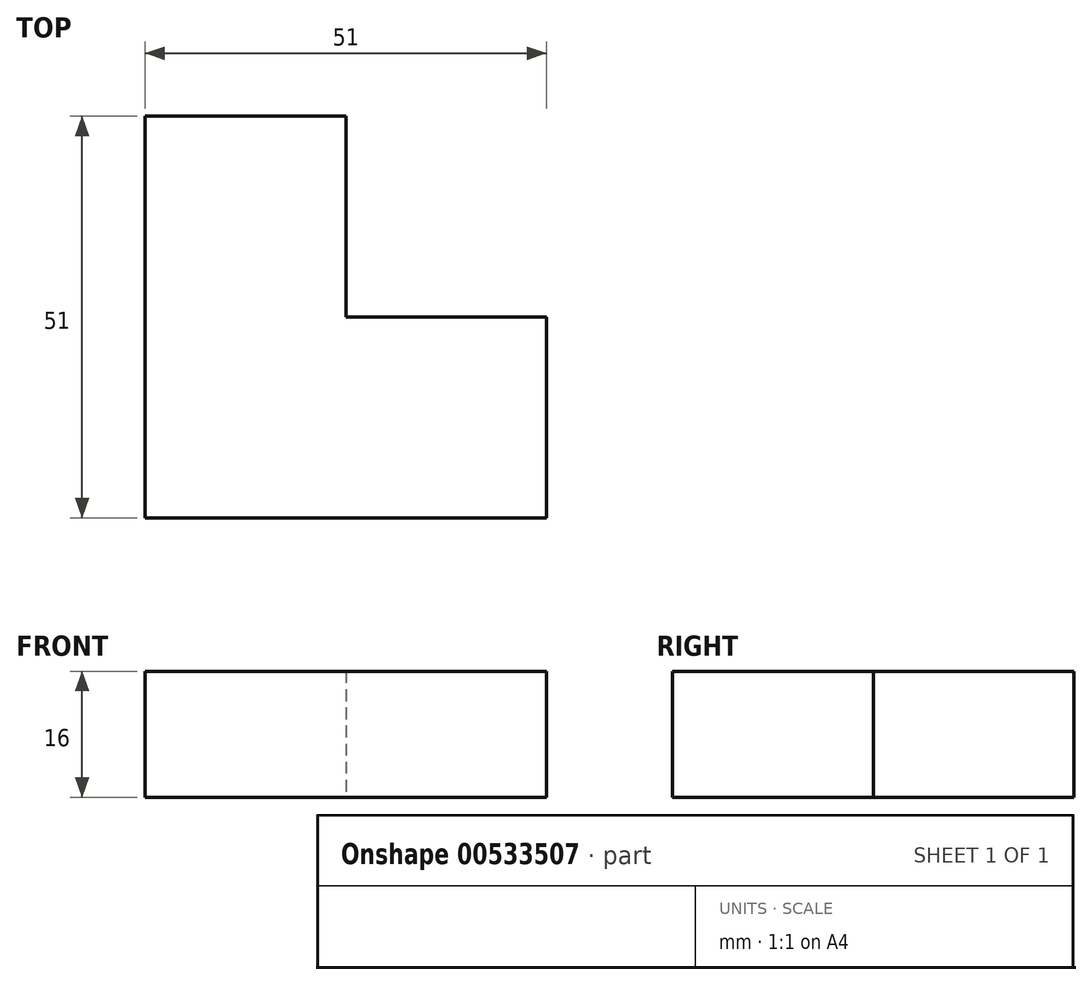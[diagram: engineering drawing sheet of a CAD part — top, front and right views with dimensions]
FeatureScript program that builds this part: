
annotation { "Feature Type Name" : "Feature", "Feature Type Description" : "" }
export const myFeature = defineFeature(function(context is Context, id is Id, definition is map)
    precondition{}
    {
        {
            var Q0;
            Q0=qCreatedBy(makeId("Top.planeOp"),FACE);
            var sketch = newSketch(context, id + "F0", { "sketchPlane" : qUnion([Q0])});
            skLineSegment(sketch, "E0.bottom", {"start": v(0, 0) * mm, "end": v(51, 0) * mm});
            skLineSegment(sketch, "E0.top", {"start": v(0, 51) * mm, "end": v(51, 51) * mm});
            skLineSegment(sketch, "E0.left", {"start": v(0, 0) * mm, "end": v(0, 51) * mm});
            skLineSegment(sketch, "E0.right", {"start": v(51, 0) * mm, "end": v(51, 51) * mm});
            skLineSegment(sketch, "E1", {"start": v(25.5, 51) * mm, "end": v(25.5, 25.5) * mm});
            skPoint(sketch, "E1.endSnap0", {"position": v(51, 25.5) * mm});
            skLineSegment(sketch, "E2", {"start": v(25.5, 25.5) * mm, "end": v(51, 25.5) * mm});
            skSolve(sketch);
        }
        {
            var Q0;
            {var subQ1=sQuery(id+"F0.wireOp",EDGE,"E0.bottom");Q0=makeQuery(id+"F0.imprint","IMPRINT",FACE,{"disambiguationData":[TD([[makeQuery(id+"F0.imprint","IMPRINT",EDGE,{"derivedFrom":subQ1}),1.0]])]});}
            extrude(context, id + "F1", {"entities" : qUnion([Q0]), "depth" : 16 * mm, "offsetDistance" : 25 * mm});
        }
    });
